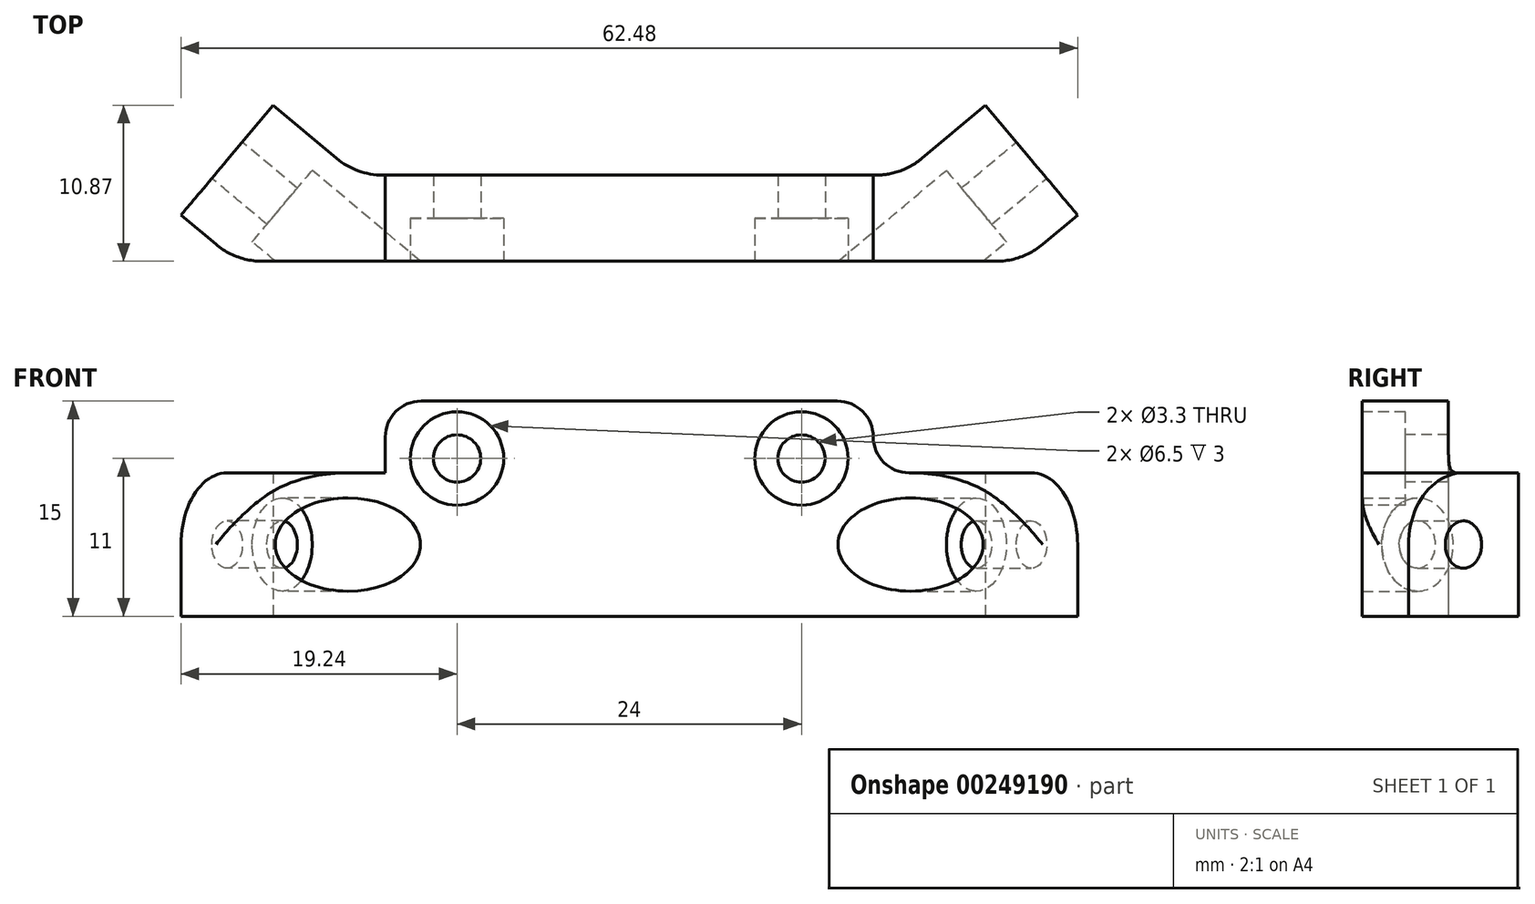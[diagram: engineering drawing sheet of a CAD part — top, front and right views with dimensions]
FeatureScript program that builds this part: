
annotation { "Feature Type Name" : "Feature", "Feature Type Description" : "" }
export const myFeature = defineFeature(function(context is Context, id is Id, definition is map)
    precondition{}
    {
        {
            var Q0;
            Q0=qCreatedBy(makeId("Top.planeOp"),FACE);
            var sketch = newSketch(context, id + "F0", { "sketchPlane" : qUnion([Q0])});
            skLineSegment(sketch, "E0", {"start": v(0, 0) * mm, "end": v(25.59, 0) * mm});
            skLineSegment(sketch, "E1", {"start": v(28.8, 1.17) * mm, "end": v(31.24, 3.21) * mm});
            skLineSegment(sketch, "E2", {"start": v(31.24, 3.21) * mm, "end": v(24.8, 10.87) * mm});
            skLineSegment(sketch, "E3", {"start": v(24.8, 10.87) * mm, "end": v(20.4, 7.17) * mm});
            skLineSegment(sketch, "E4", {"start": v(17.18, 6) * mm, "end": v(0, 6) * mm});
            skLineSegment(sketch, "E5", {"start": v(0, 6) * mm, "end": v(-17.18, 6) * mm});
            skLineSegment(sketch, "E6", {"start": v(-20.4, 7.17) * mm, "end": v(-24.8, 10.87) * mm});
            skLineSegment(sketch, "E7", {"start": v(-24.8, 10.87) * mm, "end": v(-31.24, 3.21) * mm});
            skLineSegment(sketch, "E8", {"start": v(-31.24, 3.21) * mm, "end": v(-28.8, 1.17) * mm});
            skLineSegment(sketch, "E9", {"start": v(-25.59, 0) * mm, "end": v(0, 0) * mm});
            skLineSegment(sketch, "E10", {"start": v(0, 6) * mm, "end": v(0, 0) * mm, "construction": true});
            skLineSegment(sketch, "E11", {"start": v(-17, 6) * mm, "end": v(-17, 0) * mm, "construction": true});
            skLineSegment(sketch, "E12", {"start": v(17, 6) * mm, "end": v(17, 0) * mm, "construction": true});
            skPoint(sketch, "E13.visualSharp", {"position": v(-19, 6) * mm});
            skArc(sketch, "E13.filletArc", {"start": v(-20.4, 7.17) * mm, "mid": v(-18.9, 6.3) * mm, "end": v(-17.18, 6) * mm});
            skPoint(sketch, "E14.visualSharp", {"position": v(19, 6) * mm});
            skArc(sketch, "E14.filletArc", {"start": v(17.18, 6) * mm, "mid": v(18.9, 6.3) * mm, "end": v(20.4, 7.17) * mm});
            skPoint(sketch, "E15.visualSharp", {"position": v(-27.4, 0) * mm});
            skArc(sketch, "E15.filletArc", {"start": v(-28.8, 1.17) * mm, "mid": v(-27.3, 0.3) * mm, "end": v(-25.59, 0) * mm});
            skPoint(sketch, "E16.visualSharp", {"position": v(27.4, 0) * mm});
            skArc(sketch, "E16.filletArc", {"start": v(25.59, 0) * mm, "mid": v(27.3, 0.3) * mm, "end": v(28.8, 1.17) * mm});
            skSolve(sketch);
        }
        {
            var Q0;
            Q0 = qSketchRegion(id + "F0", true);
            extrude(context, id + "F1", {"entities" : qUnion([Q0]), "depth" : 10 * mm});
        }
        {
            var Q0;
            Q0=makeQuery(id+"F1.opExtrude","CAP_FACE",FACE,{"disambiguationData":[OSD([sQuery(id+"F0.wireOp",EDGE,"E0"),sQuery(id+"F0.wireOp",EDGE,"E1"),sQuery(id+"F0.wireOp",EDGE,"E2"),sQuery(id+"F0.wireOp",EDGE,"E3"),sQuery(id+"F0.wireOp",EDGE,"E4"),sQuery(id+"F0.wireOp",EDGE,"E5"),sQuery(id+"F0.wireOp",EDGE,"E6"),sQuery(id+"F0.wireOp",EDGE,"E7"),sQuery(id+"F0.wireOp",EDGE,"E8"),sQuery(id+"F0.wireOp",EDGE,"E9"),sQuery(id+"F0.wireOp",EDGE,"E13.filletArc"),sQuery(id+"F0.wireOp",EDGE,"E14.filletArc"),sQuery(id+"F0.wireOp",EDGE,"E15.filletArc"),sQuery(id+"F0.wireOp",EDGE,"E16.filletArc")])],"isStart":false});
            var sketch = newSketch(context, id + "F2", { "sketchPlane" : qUnion([Q0])});
            skLineSegment(sketch, "E17.bottom", {"start": v(-17, 6) * mm, "end": v(17, 6) * mm});
            skLineSegment(sketch, "E17.top", {"start": v(-17, 0) * mm, "end": v(17, 0) * mm});
            skLineSegment(sketch, "E17.left", {"start": v(-17, 6) * mm, "end": v(-17, 0) * mm});
            skLineSegment(sketch, "E17.right", {"start": v(17, 6) * mm, "end": v(17, 0) * mm});
            skSolve(sketch);
        }
        {
            var Q0;
            Q0 = qSketchRegion(id + "F2", true);
            extrude(context, id + "F3", {"entities" : qUnion([Q0]), "operationType" : NewBodyOperationType.ADD, "depth" : 5 * mm});
        }
        {
            var Q0;
            Q0=makeQuery(id+"F3.boolean.opBoolean","MERGE",FACE,{"derivedFrom":[makeQuery(id+"F1.opExtrude","SWEPT_FACE",FACE,{"disambiguationData":[OSD([sQuery(id+"F0.wireOp",EDGE,"E0"),sQuery(id+"F0.wireOp",EDGE,"E9")])]}),makeQuery(id+"F3.opExtrude","SWEPT_FACE",FACE,{"disambiguationData":[OSD([sQuery(id+"F2.wireOp",EDGE,"E17.top")])]})]});
            var sketch = newSketch(context, id + "F4", { "sketchPlane" : qUnion([Q0])});
            skLineSegment(sketch, "E18", {"start": v(-17, 11) * mm, "end": v(17, 11) * mm, "construction": true});
            skPoint(sketch, "E19", {"position": v(-12, 11) * mm});
            skPoint(sketch, "E20", {"position": v(12, 11) * mm});
            skSolve(sketch);
        }
        {
            var Q0;
            Q0=makeQuery(id+"F3.opExtrude","CAP_EDGE",EDGE,{"disambiguationData":[OSD([sQuery(id+"F2.wireOp",EDGE,"E17.right")])],"isStart":true});
            var Q1;
            Q1=makeQuery(id+"F3.opExtrude","CAP_EDGE",EDGE,{"disambiguationData":[OSD([sQuery(id+"F2.wireOp",EDGE,"E17.right")])],"isStart":false});
            var Q2;
            Q2=makeQuery(id+"F3.opExtrude","CAP_EDGE",EDGE,{"disambiguationData":[OSD([sQuery(id+"F2.wireOp",EDGE,"E17.left")])],"isStart":false});
            var Q3;
            Q3=makeQuery(id+"F3.opExtrude","CAP_EDGE",EDGE,{"disambiguationData":[OSD([sQuery(id+"F2.wireOp",EDGE,"E17.left")])],"isStart":true});
            fillet(context, id + "F5", {"entities" : qUnion([Q0, Q1, Q2, Q3]), "radius" : 2.5 * mm, "tangentPropagation" : true, "allowEdgeOverflow" : false});
        }
        {
            var Q0;
            Q0=sQuery(id+"F4.wireOp",VERTEX,"E19");
            var Q1;
            Q1=sQuery(id+"F4.wireOp",VERTEX,"E20");
            var Q2;
            Q2=makeQuery(id+"F1.opExtrude","SWEPT_BODY",BODY,{"disambiguationData":[OSD([sQuery(id+"F0.wireOp",EDGE,"E0"),sQuery(id+"F0.wireOp",EDGE,"E1"),sQuery(id+"F0.wireOp",EDGE,"E2"),sQuery(id+"F0.wireOp",EDGE,"E3"),sQuery(id+"F0.wireOp",EDGE,"E4"),sQuery(id+"F0.wireOp",EDGE,"E5"),sQuery(id+"F0.wireOp",EDGE,"E6"),sQuery(id+"F0.wireOp",EDGE,"E7"),sQuery(id+"F0.wireOp",EDGE,"E8"),sQuery(id+"F0.wireOp",EDGE,"E9"),sQuery(id+"F0.wireOp",EDGE,"E13.filletArc"),sQuery(id+"F0.wireOp",EDGE,"E14.filletArc"),sQuery(id+"F0.wireOp",EDGE,"E15.filletArc"),sQuery(id+"F0.wireOp",EDGE,"E16.filletArc")])]});
            hole(context, id + "F6", {"style" : HoleStyle.C_BORE, "endStyle" : HoleEndStyle.THROUGH, "standardTappedOrClearance" : lookupTablePath({ "standard" : "ISO", "fit" : "Normal", "size" : "M3", "type" : "Clearance" }), "standardBlindInLast" : lookupTablePath({ "fit" : "Standard", "standard" : "ISO", "size" : "M3", "type" : "Clearance" }), "holeDiameter" : 3.3 * mm, "cBoreDiameter" : 6.5 * mm, "cBoreDepth" : 3 * mm, "tappedDepth" : 5.75 * mm, "tapClearance" : 3, "startFromSketch" : true, "locations" : qUnion([Q0, Q1]), "scope" : qUnion([Q2])});
        }
        {
            var Q0;
            Q0=makeQuery(id+"F1.opExtrude","CAP_EDGE",EDGE,{"disambiguationData":[OSD([sQuery(id+"F0.wireOp",EDGE,"E8")])],"isStart":false});
            var Q1;
            Q1=makeQuery(id+"F1.opExtrude","CAP_EDGE",EDGE,{"disambiguationData":[OSD([sQuery(id+"F0.wireOp",EDGE,"E1")])],"isStart":false});
            fillet(context, id + "F7", {"entities" : qUnion([Q0, Q1]), "radius" : 5 * mm, "allowEdgeOverflow" : false});
        }
        {
            var Q0;
            Q0=makeQuery(id+"F1.opExtrude","SWEPT_FACE",FACE,{"disambiguationData":[OSD([sQuery(id+"F0.wireOp",EDGE,"E2")])]});
            var sketch = newSketch(context, id + "F8", { "sketchPlane" : qUnion([Q0])});
            skLineSegment(sketch, "E21", {"start": v(-7.62, 10) * mm, "end": v(-17.62, 0) * mm, "construction": true});
            skCircle(sketch, "E22", {"center": v(-12.62, 5) * mm, "radius": 1.65 * mm});
            skSolve(sketch);
        }
        {
            var Q0;
            Q0 = qSketchRegion(id + "F8", true);
            extrude(context, id + "F9", {"entities" : qUnion([Q0]), "operationType" : NewBodyOperationType.REMOVE, "endBound" : BoundingType.THROUGH_ALL, "oppositeDirection" : true, "depth" : 25 * mm});
        }
        {
            var Q0;
            Q0=makeQuery(id+"F1.opExtrude","SWEPT_FACE",FACE,{"disambiguationData":[OSD([sQuery(id+"F0.wireOp",EDGE,"E7")])]});
            var sketch = newSketch(context, id + "F10", { "sketchPlane" : qUnion([Q0])});
            skLineSegment(sketch, "E23", {"start": v(7.62, 10) * mm, "end": v(17.62, 0) * mm, "construction": true});
            skCircle(sketch, "E24", {"center": v(12.62, 5) * mm, "radius": 1.65 * mm});
            skSolve(sketch);
        }
        {
            var Q0;
            Q0 = qSketchRegion(id + "F10", true);
            extrude(context, id + "F11", {"entities" : qUnion([Q0]), "operationType" : NewBodyOperationType.REMOVE, "endBound" : BoundingType.THROUGH_ALL, "oppositeDirection" : true, "depth" : 25 * mm});
        }
        {
            var Q0;
            Q0=makeQuery(id+"F1.opExtrude","SWEPT_FACE",FACE,{"disambiguationData":[OSD([sQuery(id+"F0.wireOp",EDGE,"E2")])]});
            cPlane(context, id + "F12", {"entities" : qUnion([Q0]), "cplaneType" : CPlaneType.OFFSET, "offset" : 5 * mm, "oppositeDirection" : true, "width" : 150 * mm, "height" : 150 * mm});
        }
        {
            var Q0;
            Q0=qCreatedBy(id+"F12.planeOp",FACE);
            var sketch = newSketch(context, id + "F13", { "sketchPlane" : qUnion([Q0])});
            skCircle(sketch, "E25", {"center": v(-12.6, 5) * mm, "radius": 3.25 * mm});
            skLineSegment(sketch, "E26", {"start": v(-12.6, 5) * mm, "end": v(-12.6, 0) * mm, "construction": true});
            skLineSegment(sketch, "E27", {"start": v(-12.6, 0) * mm, "end": v(0, 0) * mm, "construction": true});
            skSolve(sketch);
        }
        {
            var Q0;
            Q0 = qSketchRegion(id + "F13", true);
            extrude(context, id + "F14", {"entities" : qUnion([Q0]), "operationType" : NewBodyOperationType.REMOVE, "oppositeDirection" : true, "depth" : 25 * mm});
        }
        {
            var Q0;
            Q0=makeQuery(id+"F1.opExtrude","SWEPT_FACE",FACE,{"disambiguationData":[OSD([sQuery(id+"F0.wireOp",EDGE,"E7")])]});
            cPlane(context, id + "F15", {"entities" : qUnion([Q0]), "cplaneType" : CPlaneType.OFFSET, "offset" : 5 * mm, "oppositeDirection" : true, "width" : 150 * mm, "height" : 150 * mm});
        }
        {
            var Q0;
            Q0=qCreatedBy(id+"F15.planeOp",FACE);
            var sketch = newSketch(context, id + "F16", { "sketchPlane" : qUnion([Q0])});
            skCircle(sketch, "E28", {"center": v(12.6, 5) * mm, "radius": 3.25 * mm});
            skLineSegment(sketch, "E29", {"start": v(12.6, 5) * mm, "end": v(12.6, 0) * mm, "construction": true});
            skLineSegment(sketch, "E30", {"start": v(12.6, 0) * mm, "end": v(0, 0) * mm, "construction": true});
            skSolve(sketch);
        }
        {
            var Q0;
            Q0 = qSketchRegion(id + "F16", true);
            extrude(context, id + "F17", {"entities" : qUnion([Q0]), "operationType" : NewBodyOperationType.REMOVE, "oppositeDirection" : true, "depth" : 25 * mm});
        }
    });
